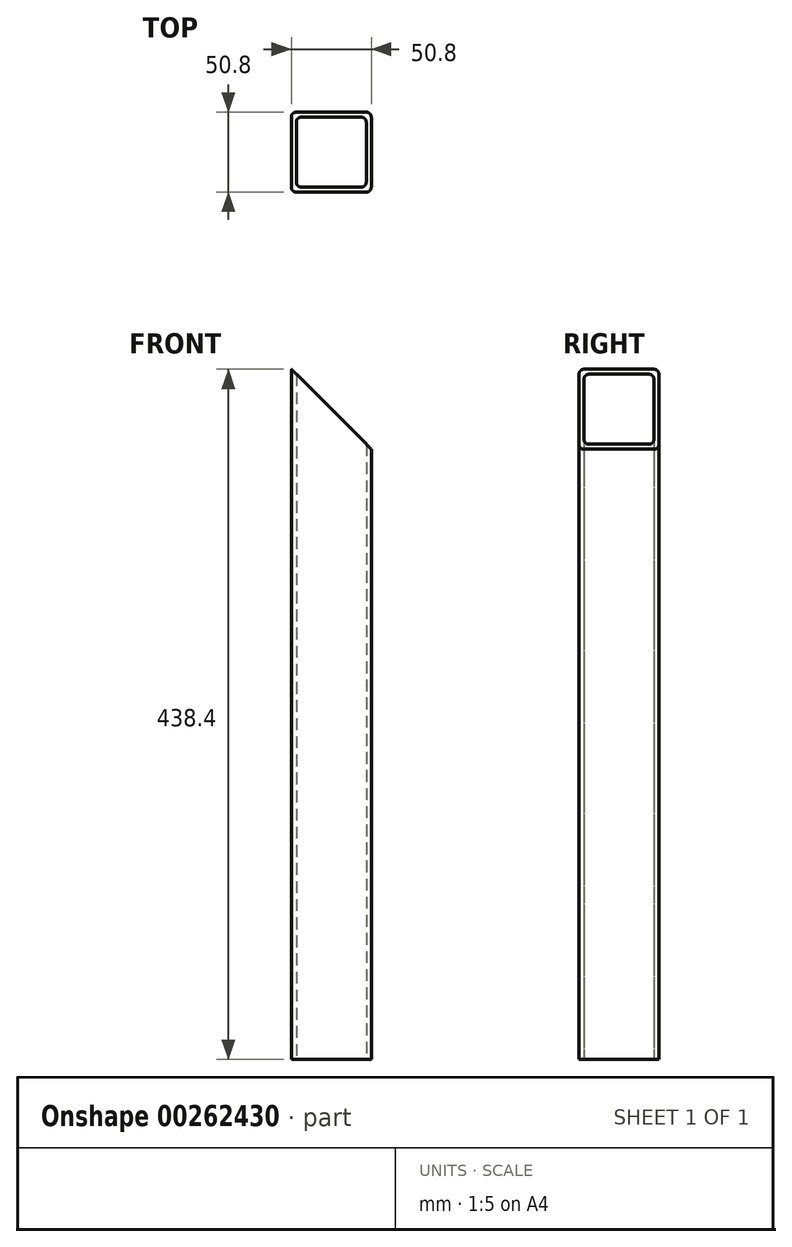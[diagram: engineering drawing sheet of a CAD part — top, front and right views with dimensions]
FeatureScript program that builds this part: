
annotation { "Feature Type Name" : "Feature", "Feature Type Description" : "" }
export const myFeature = defineFeature(function(context is Context, id is Id, definition is map)
    precondition{}
    {
        {
            var Q0;
            Q0=qCreatedBy(makeId("Top.planeOp"),FACE);
            var sketch = newSketch(context, id + "F0", { "sketchPlane" : qUnion([Q0])});
            skLineSegment(sketch, "E0.bottom", {"start": v(22.23, 25.4) * mm, "end": v(-22.23, 25.4) * mm});
            skLineSegment(sketch, "E0.top", {"start": v(22.23, -25.4) * mm, "end": v(-22.23, -25.4) * mm});
            skLineSegment(sketch, "E0.left", {"start": v(25.4, 22.23) * mm, "end": v(25.4, -22.23) * mm});
            skLineSegment(sketch, "E0.right", {"start": v(-25.4, 22.23) * mm, "end": v(-25.4, -22.23) * mm});
            skPoint(sketch, "E0.middle", {"position": v(0, 0) * mm});
            skLineSegment(sketch, "E1.bottom", {"start": v(19.05, 22.23) * mm, "end": v(-19.05, 22.23) * mm});
            skLineSegment(sketch, "E1.top", {"start": v(19.05, -22.23) * mm, "end": v(-19.05, -22.23) * mm});
            skLineSegment(sketch, "E1.left", {"start": v(22.23, 19.05) * mm, "end": v(22.23, -19.05) * mm});
            skLineSegment(sketch, "E1.right", {"start": v(-22.23, 19.05) * mm, "end": v(-22.23, -19.05) * mm});
            skPoint(sketch, "E2.visualSharp", {"position": v(-22.23, 22.23) * mm});
            skArc(sketch, "E2.filletArc", {"start": v(-19.05, 22.23) * mm, "mid": v(-21.3, 21.3) * mm, "end": v(-22.23, 19.05) * mm});
            skPoint(sketch, "E3.visualSharp", {"position": v(-25.4, 25.4) * mm});
            skArc(sketch, "E3.filletArc", {"start": v(-22.23, 25.4) * mm, "mid": v(-24.47, 24.47) * mm, "end": v(-25.4, 22.23) * mm});
            skPoint(sketch, "E4.visualSharp", {"position": v(-22.23, -22.23) * mm});
            skArc(sketch, "E4.filletArc", {"start": v(-22.23, -19.05) * mm, "mid": v(-21.3, -21.3) * mm, "end": v(-19.05, -22.23) * mm});
            skPoint(sketch, "E5.visualSharp", {"position": v(-25.4, -25.4) * mm});
            skArc(sketch, "E5.filletArc", {"start": v(-25.4, -22.23) * mm, "mid": v(-24.47, -24.47) * mm, "end": v(-22.23, -25.4) * mm});
            skPoint(sketch, "E6.visualSharp", {"position": v(22.23, 22.23) * mm});
            skArc(sketch, "E6.filletArc", {"start": v(22.23, 19.05) * mm, "mid": v(21.3, 21.3) * mm, "end": v(19.05, 22.23) * mm});
            skPoint(sketch, "E7.visualSharp", {"position": v(25.4, 25.4) * mm});
            skArc(sketch, "E7.filletArc", {"start": v(25.4, 22.23) * mm, "mid": v(24.47, 24.47) * mm, "end": v(22.23, 25.4) * mm});
            skPoint(sketch, "E8.visualSharp", {"position": v(22.23, -22.23) * mm});
            skArc(sketch, "E8.filletArc", {"start": v(19.05, -22.23) * mm, "mid": v(21.3, -21.3) * mm, "end": v(22.23, -19.05) * mm});
            skPoint(sketch, "E9.visualSharp", {"position": v(25.4, -25.4) * mm});
            skArc(sketch, "E9.filletArc", {"start": v(22.23, -25.4) * mm, "mid": v(24.47, -24.47) * mm, "end": v(25.4, -22.23) * mm});
            skSolve(sketch);
        }
        {
            var Q0;
            Q0 = qSketchRegion(id + "F0", true);
            extrude(context, id + "F1", {"entities" : qUnion([Q0]), "depth" : 438.4 * mm});
        }
        {
            var Q0;
            Q0=qCreatedBy(makeId("Front.planeOp"),FACE);
            var sketch = newSketch(context, id + "F2", { "sketchPlane" : qUnion([Q0])});
            skLineSegment(sketch, "E10.bottom", {"start": v(25.4, 438.4) * mm, "end": v(-25.4, 438.4) * mm});
            skLineSegment(sketch, "E10.left", {"start": v(25.4, 438.4) * mm, "end": v(25.4, 387.6) * mm});
            skPoint(sketch, "E10.middle", {"position": v(0, 413) * mm});
            skLineSegment(sketch, "E11", {"start": v(-25.4, 438.4) * mm, "end": v(25.4, 387.6) * mm});
            skPoint(sketch, "E10.top.end.orphan", {"position": v(-25.4, 387.6) * mm});
            skSolve(sketch);
        }
        {
            var Q0;
            Q0 = qSketchRegion(id + "F2", true);
            extrude(context, id + "F3", {"entities" : qUnion([Q0]), "operationType" : NewBodyOperationType.REMOVE, "depth" : 25.4 * mm, "hasSecondDirection" : true, "secondDirectionOppositeDirection" : true, "secondDirectionDepth" : 25.4 * mm});
        }
    });
